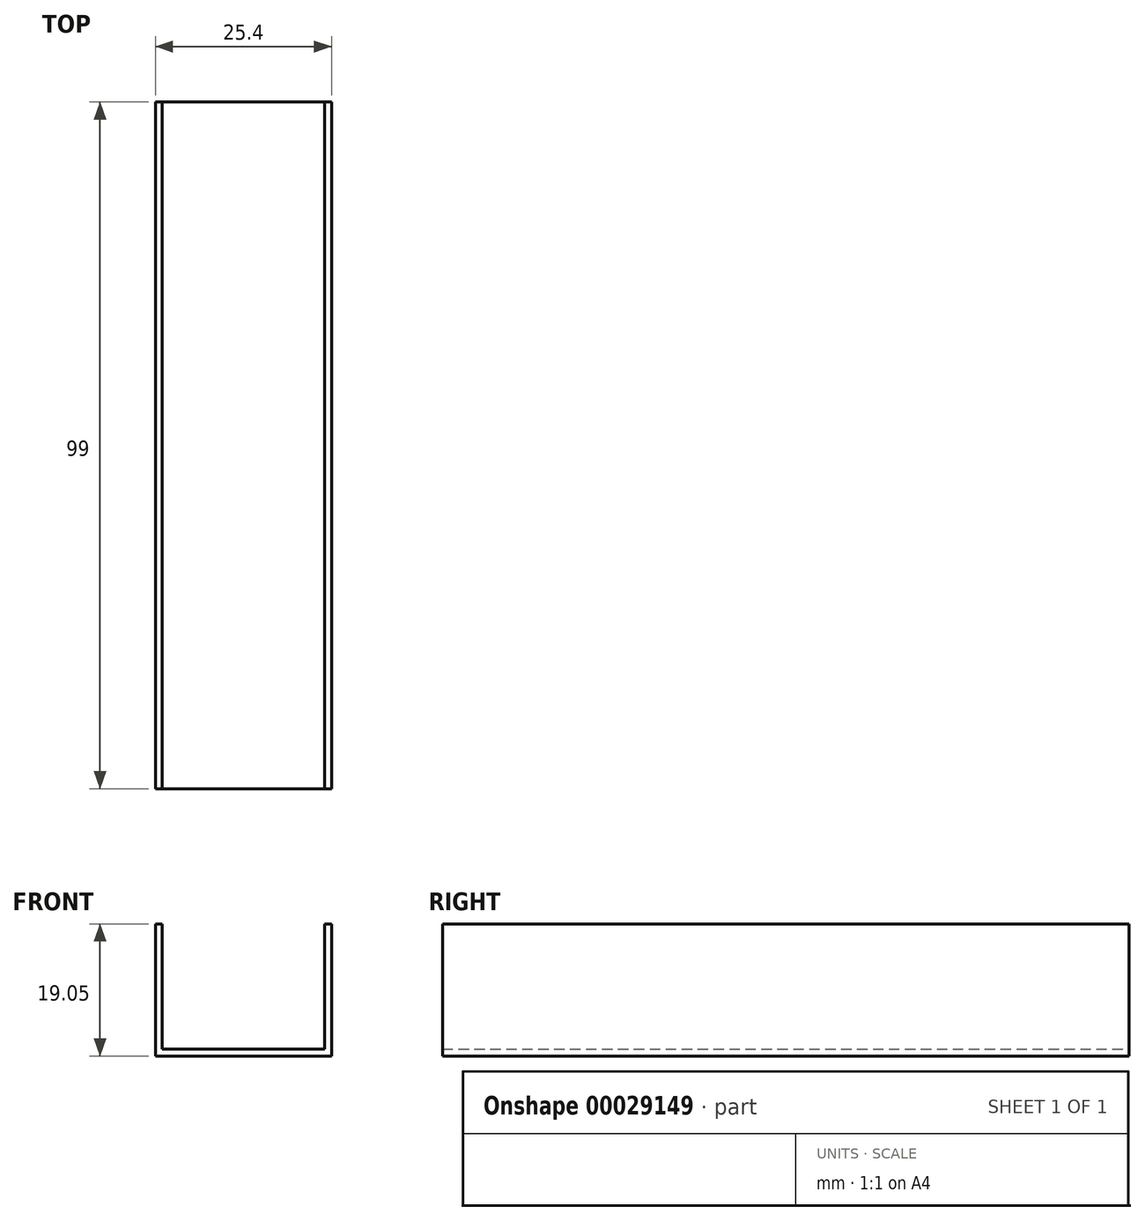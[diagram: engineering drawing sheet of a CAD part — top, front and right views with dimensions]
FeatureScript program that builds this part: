
annotation { "Feature Type Name" : "Feature", "Feature Type Description" : "" }
export const myFeature = defineFeature(function(context is Context, id is Id, definition is map)
    precondition{}
    {
        {
            var Q0;
            Q0=qCreatedBy(makeId("Front.planeOp"),FACE);
            var sketch = newSketch(context, id + "F0", { "sketchPlane" : qUnion([Q0])});
            skLineSegment(sketch, "E0", {"start": v(-12.7, 0) * mm, "end": v(0, 0) * mm});
            skLineSegment(sketch, "E1", {"start": v(0, 0) * mm, "end": v(0, 1) * mm});
            skLineSegment(sketch, "E2", {"start": v(0, 1) * mm, "end": v(-11.7, 1) * mm});
            skLineSegment(sketch, "E3", {"start": v(-11.7, 1) * mm, "end": v(-11.7, 19.05) * mm});
            skLineSegment(sketch, "E4", {"start": v(-12.7, 0) * mm, "end": v(-12.7, 19.05) * mm});
            skLineSegment(sketch, "E5", {"start": v(-12.7, 19.05) * mm, "end": v(-11.7, 19.05) * mm});
            skLineSegment(sketch, "E6.MirrorCS", {"start": v(12.7, 19.05) * mm, "end": v(11.7, 19.05) * mm});
            skLineSegment(sketch, "E7.MirrorCS", {"start": v(12.7, 0) * mm, "end": v(12.7, 19.05) * mm});
            skLineSegment(sketch, "E8.MirrorCS", {"start": v(11.7, 1) * mm, "end": v(11.7, 19.05) * mm});
            skLineSegment(sketch, "E9.MirrorCS", {"start": v(12.7, 0) * mm, "end": v(0, 0) * mm});
            skLineSegment(sketch, "E10.MirrorCS", {"start": v(0, 1) * mm, "end": v(11.7, 1) * mm});
            skSolve(sketch);
        }
        {
            var Q0;
            Q0 = qSketchRegion(id + "F0", true);
            extrude(context, id + "F1", {"entities" : qUnion([Q0]), "depth" : 99 * mm});
        }
    });
